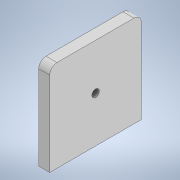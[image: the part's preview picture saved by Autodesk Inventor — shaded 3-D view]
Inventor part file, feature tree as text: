
AUTODESK INVENTOR PART (.ipt)
format: ipt  version: 2021 (Build 250183000, 183)  size: 112,128 bytes
history: native  units: mm
features: sketch x2, extrude x1, hole x1, fillet x1
ambient origin geometry x8: Origin, YZ Plane, XZ Plane, XY Plane, X Axis, Y Axis, Z Axis, Center Point
bodies: Solid1 (feature_tree)
feature tree (5):
  extrude  "Extrusion1"  Depth=50.0mm
  hole  "Hole1"  [1 undecoded]
  fillet  "Fillet1"  Radius=6.0mm
  sketch  "Sketch1"  dims[d0=50.0mm d1=50.0mm]
  sketch  "Sketch2"  dims[d2=25.0mm d3=25.0mm d4=6.0mm d5=0.0mm d6=4.0mm d7=6.0mm d8=4.0mm d9=2.0mm d10=90.0deg d11=8.0mm d12=20.594885mm d13=4.0mm]
note: 1 required parameter value undecoded (feature->parameter linkage not recoverable at this tier; creation-order binding heuristic only, values carry confidence <= 0.55)
